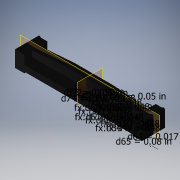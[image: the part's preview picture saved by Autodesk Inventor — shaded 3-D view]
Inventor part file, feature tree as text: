
AUTODESK INVENTOR PART (.ipt)
format: ipt  version: 2019 (Build 230136000, 136)  size: 235,520 bytes
history: native  units: mm (DEFAULTED — no unit token found)
features: sketch x8, extrude x5, fillet x1
ambient origin geometry x8: Origin, YZ Plane, XZ Plane, XY Plane, X Axis, Y Axis, Z Axis, Center Point
bodies: Solid1 (feature_tree)
feature tree (14):
  extrude  "Extrusion1"  Depth=10.0mm
  extrude  "Extrusion2"  Depth=47.0mm
  extrude  "Extrusion3"  Depth=7.4676mm TaperAngle=0.0deg
  extrude  "Extrusion4"  Depth=2.54mm
  extrude  "Extrusion5"  Depth=1.3208mm
  fillet  "Fillet1"  Radius=0.762mm
  sketch  "Sketch8"  dims[d15=8.128mm]
  sketch  "Sketch9"  dims[d16=16.891mm]
  sketch  "Sketch11"  dims[d17=0.508mm d18=3.302mm d19=0.0mm d20=1.143mm d21=3.302mm d22=0.0mm d23=0.5842mm d37=0.508mm d38=0.5842mm d39=0.254mm d40=160.0mm d42=1.27mm d43=10.0mm d45=25.4mm d48=1.27mm d49=1.27mm d50=1.27mm d51=1.27mm d53=1.27mm d54=1.27mm d55=1.27mm d56=1.27mm d57=1.27mm d58=1.27mm d59=1.27mm d60=1.27mm d61=1.27mm d62=1.27mm d64=0.4318mm d65=2.032mm d72=1.27mm d73=1.27mm d74=0.4318mm]
  sketch  "Sketch1"  dims[d0=55.0mm d1=10.0mm]
  sketch  "Sketch2"  dims[d2=7.4676mm d3=0.0mm d4=47.0mm]
  sketch  "Sketch3"  dims[d5=0.5842mm d6=7.4676mm d7=0.0mm]
  sketch  "Sketch4"  dims[d8=47.0mm d9=2.54mm]
  sketch  "Sketch5"  dims[d11=7.4676mm d12=0.0mm d13=1.3208mm d14=0.762mm]
